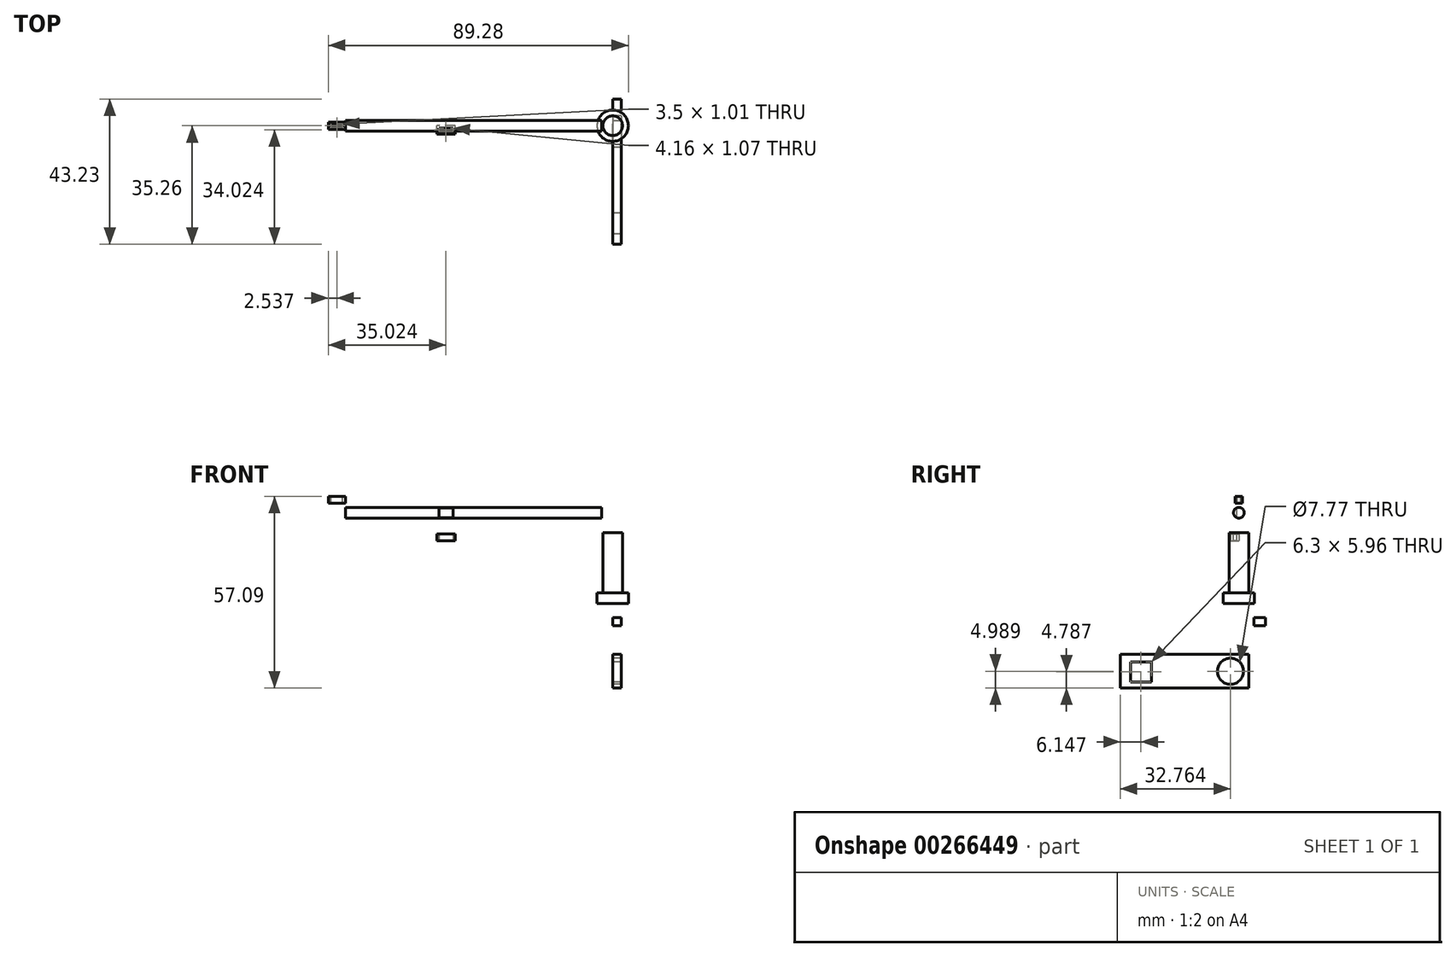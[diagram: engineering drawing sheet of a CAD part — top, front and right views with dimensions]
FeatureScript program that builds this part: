
annotation { "Feature Type Name" : "Feature", "Feature Type Description" : "" }
export const myFeature = defineFeature(function(context is Context, id is Id, definition is map)
    precondition{}
    {
        {
            var Q0;
            Q0=qCreatedBy(makeId("Front.planeOp"),FACE);
            var sketch = newSketch(context, id + "F0", { "sketchPlane" : qUnion([Q0])});
            skLineSegment(sketch, "E0.bottom", {"start": v(-4.66, 21.15) * mm, "end": v(0, 21.15) * mm});
            skLineSegment(sketch, "E0.top", {"start": v(-4.66, 0) * mm, "end": v(0, 0) * mm});
            skLineSegment(sketch, "E0.left", {"start": v(-4.66, 21.15) * mm, "end": v(-4.66, 0) * mm});
            skLineSegment(sketch, "E0.right", {"start": v(0, 21.15) * mm, "end": v(0, 0) * mm});
            skSolve(sketch);
        }
        {
            var Q0;
            Q0=makeQuery(id+"F0.imprint","IMPRINT",FACE,{"disambiguationData":[TD([[makeQuery(id+"F0.imprint","IMPRINT",EDGE,{"derivedFrom":sQuery(id+"F0.wireOp",EDGE,"E0.bottom")}),-1.0]])]});
            var Q1;
            Q1=sQuery(id+"F0.wireOp",EDGE,"E0.right");
            revolve(context, id + "F1", {"entities" : qUnion([Q0]), "axis" : qUnion([Q1]), "revolveType" : RevolveType.FULL});
        }
        {
            var Q0;
            Q0=qCreatedBy(makeId("Front.planeOp"),FACE);
            var sketch = newSketch(context, id + "F2", { "sketchPlane" : qUnion([Q0])});
            skLineSegment(sketch, "E1.bottom", {"start": v(-79.54, 28.67) * mm, "end": v(-3.34, 28.67) * mm});
            skLineSegment(sketch, "E1.top", {"start": v(-79.54, 27.07) * mm, "end": v(-3.34, 27.07) * mm});
            skLineSegment(sketch, "E1.left", {"start": v(-79.54, 28.67) * mm, "end": v(-79.54, 27.07) * mm});
            skLineSegment(sketch, "E1.right", {"start": v(-3.34, 28.67) * mm, "end": v(-3.34, 27.07) * mm});
            skSolve(sketch);
        }
        {
            var Q0;
            Q0=makeQuery(id+"F2.imprint","IMPRINT",FACE,{"disambiguationData":[TD([[makeQuery(id+"F2.imprint","IMPRINT",EDGE,{"derivedFrom":sQuery(id+"F2.wireOp",EDGE,"E1.bottom")}),-1.0]])]});
            var Q1;
            Q1=sQuery(id+"F2.wireOp",EDGE,"E1.top");
            revolve(context, id + "F3", {"entities" : qUnion([Q0]), "axis" : qUnion([Q1]), "revolveType" : RevolveType.FULL});
        }
        {
            var Q0;
            Q0=qCreatedBy(makeId("Front.planeOp"),FACE);
            var sketch = newSketch(context, id + "F4", { "sketchPlane" : qUnion([Q0])});
            skLineSegment(sketch, "E2.bottom", {"start": v(2.93, 21.6) * mm, "end": v(5.43, 21.6) * mm});
            skLineSegment(sketch, "E2.top", {"start": v(2.93, 3.28) * mm, "end": v(5.43, 3.28) * mm});
            skLineSegment(sketch, "E2.left", {"start": v(2.93, 21.6) * mm, "end": v(2.93, 3.28) * mm});
            skLineSegment(sketch, "E2.right", {"start": v(5.43, 21.6) * mm, "end": v(5.43, 3.28) * mm});
            skSolve(sketch);
        }
        {
            var Q0;
            Q0=makeQuery(id+"F4.imprint","IMPRINT",FACE,{"disambiguationData":[TD([[makeQuery(id+"F4.imprint","IMPRINT",EDGE,{"derivedFrom":sQuery(id+"F4.wireOp",EDGE,"E2.bottom")}),-1.0]])]});
            var Q1;
            Q1=makeQuery(id+"F1.opRevolve","SWEPT_FACE",FACE,{"disambiguationData":[OSD([sQuery(id+"F0.wireOp",EDGE,"E0.left")])]});
            revolve(context, id + "F5", {"operationType" : NewBodyOperationType.REMOVE, "entities" : qUnion([Q0]), "axis" : qUnion([Q1]), "revolveType" : RevolveType.FULL, "oppositeDirection" : true});
        }
        {
            var Q0;
            Q0=makeQuery(id+"F3.opRevolve","SWEPT_FACE",FACE,{"disambiguationData":[OSD([sQuery(id+"F2.wireOp",EDGE,"E1.left")])]});
            var sketch = newSketch(context, id + "F6", { "sketchPlane" : qUnion([Q0])});
            skLineSegment(sketch, "E3.bottom", {"start": v(-1.06, 32) * mm, "end": v(1.16, 32) * mm});
            skLineSegment(sketch, "E3.top", {"start": v(-1.06, 29.89) * mm, "end": v(1.16, 29.89) * mm});
            skLineSegment(sketch, "E3.left", {"start": v(-1.06, 32) * mm, "end": v(-1.06, 29.89) * mm});
            skLineSegment(sketch, "E3.right", {"start": v(1.16, 32) * mm, "end": v(1.16, 29.89) * mm});
            skSolve(sketch);
        }
        {
            var Q0;
            Q0=makeQuery(id+"F6.imprint","IMPRINT",FACE,{"disambiguationData":[TD([[makeQuery(id+"F6.imprint","IMPRINT",EDGE,{"derivedFrom":sQuery(id+"F6.wireOp",EDGE,"E3.bottom")}),-1.0]])]});
            extrude(context, id + "F7", {"entities" : qUnion([Q0]), "operationType" : NewBodyOperationType.ADD, "depth" : 5.08 * mm});
        }
        {
            var Q0;
            Q0=makeQuery(id+"F7.opExtrude","SWEPT_FACE",FACE,{"disambiguationData":[OSD([sQuery(id+"F6.wireOp",EDGE,"E3.bottom")])]});
            var sketch = newSketch(context, id + "F8", { "sketchPlane" : qUnion([Q0])});
            skLineSegment(sketch, "E4.bottom", {"start": v(-83.84, 0.5) * mm, "end": v(-80.33, 0.5) * mm});
            skLineSegment(sketch, "E4.top", {"start": v(-83.84, -0.5) * mm, "end": v(-80.33, -0.5) * mm});
            skLineSegment(sketch, "E4.left", {"start": v(-83.84, 0.5) * mm, "end": v(-83.84, -0.5) * mm});
            skLineSegment(sketch, "E4.right", {"start": v(-80.33, 0.5) * mm, "end": v(-80.33, -0.5) * mm});
            skPoint(sketch, "E4.middle", {"position": v(-82.08, 0) * mm});
            skPoint(sketch, "E4.middle.positionSnap0", {"position": v(-82.08, -1.16) * mm});
            skPoint(sketch, "E4.centerSnap0", {"position": v(-82.08, -1.16) * mm});
            skSolve(sketch);
        }
        {
            var Q0;
            Q0=makeQuery(id+"F8.imprint","IMPRINT",FACE,{"disambiguationData":[TD([[makeQuery(id+"F8.imprint","IMPRINT",EDGE,{"derivedFrom":sQuery(id+"F8.wireOp",EDGE,"E4.bottom")}),-1.0]])]});
            extrude(context, id + "F9", {"entities" : qUnion([Q0]), "operationType" : NewBodyOperationType.REMOVE, "endBound" : BoundingType.THROUGH_ALL, "oppositeDirection" : true, "depth" : 25.4 * mm});
        }
        {
            var Q0;
            Q0=qCreatedBy(makeId("Right.planeOp"),FACE);
            var sketch = newSketch(context, id + "F10", { "sketchPlane" : qUnion([Q0])});
            skLineSegment(sketch, "E5.bottom", {"start": v(3.02, -15.1) * mm, "end": v(-35.26, -15.1) * mm});
            skLineSegment(sketch, "E5.top", {"start": v(3.02, -25.1) * mm, "end": v(-35.26, -25.1) * mm});
            skLineSegment(sketch, "E5.left", {"start": v(3.02, -15.1) * mm, "end": v(3.02, -25.1) * mm});
            skLineSegment(sketch, "E5.right", {"start": v(-35.26, -15.1) * mm, "end": v(-35.26, -25.1) * mm});
            skCircle(sketch, "E6", {"center": v(-2.5, -20.1) * mm, "radius": 3.89 * mm});
            skLineSegment(sketch, "E7.bottom", {"start": v(-32.26, -17.33) * mm, "end": v(-25.96, -17.33) * mm});
            skLineSegment(sketch, "E7.top", {"start": v(-32.26, -23.28) * mm, "end": v(-25.96, -23.28) * mm});
            skLineSegment(sketch, "E7.left", {"start": v(-32.26, -17.33) * mm, "end": v(-32.26, -23.28) * mm});
            skLineSegment(sketch, "E7.right", {"start": v(-25.96, -17.33) * mm, "end": v(-25.96, -23.28) * mm});
            skSolve(sketch);
        }
        {
            var Q0;
            Q0 = qSketchRegion(id + "F10", true);
            extrude(context, id + "F11", {"entities" : qUnion([Q0]), "depth" : 2.54 * mm});
        }
        {
            var Q0;
            Q0=qCreatedBy(makeId("Right.planeOp"),FACE);
            var sketch = newSketch(context, id + "F12", { "sketchPlane" : qUnion([Q0])});
            skLineSegment(sketch, "E8.bottom", {"start": v(4.47, -4.08) * mm, "end": v(7.97, -4.08) * mm});
            skLineSegment(sketch, "E8.top", {"start": v(4.47, -6.57) * mm, "end": v(7.97, -6.57) * mm});
            skLineSegment(sketch, "E8.left", {"start": v(4.47, -4.08) * mm, "end": v(4.47, -6.57) * mm});
            skLineSegment(sketch, "E8.right", {"start": v(7.97, -4.08) * mm, "end": v(7.97, -6.57) * mm});
            skSolve(sketch);
        }
        {
            var Q0;
            Q0=makeQuery(id+"F12.imprint","IMPRINT",FACE,{"disambiguationData":[TD([[makeQuery(id+"F12.imprint","IMPRINT",EDGE,{"derivedFrom":sQuery(id+"F12.wireOp",EDGE,"E8.bottom")}),-1.0]])]});
            extrude(context, id + "F13", {"entities" : qUnion([Q0]), "depth" : 2.54 * mm});
        }
        {
            var Q0;
            Q0=qCreatedBy(makeId("Front.planeOp"),FACE);
            var sketch = newSketch(context, id + "F14", { "sketchPlane" : qUnion([Q0])});
            skLineSegment(sketch, "E9.bottom", {"start": v(-46.86, 20.72) * mm, "end": v(-52.33, 20.72) * mm});
            skLineSegment(sketch, "E9.top", {"start": v(-46.86, 18.68) * mm, "end": v(-52.33, 18.68) * mm});
            skLineSegment(sketch, "E9.left", {"start": v(-46.86, 20.72) * mm, "end": v(-46.86, 18.68) * mm});
            skLineSegment(sketch, "E9.right", {"start": v(-52.33, 20.72) * mm, "end": v(-52.33, 18.68) * mm});
            skSolve(sketch);
        }
        {
            var Q0;
            Q0=makeQuery(id+"F14.imprint","IMPRINT",FACE,{"disambiguationData":[TD([[makeQuery(id+"F14.imprint","IMPRINT",EDGE,{"derivedFrom":sQuery(id+"F14.wireOp",EDGE,"E9.bottom")}),1.0]])]});
            extrude(context, id + "F15", {"entities" : qUnion([Q0]), "depth" : 2.54 * mm});
        }
        {
            var Q0;
            Q0=makeQuery(id+"F15.opExtrude","SWEPT_FACE",FACE,{"disambiguationData":[OSD([sQuery(id+"F14.wireOp",EDGE,"E9.top")])]});
            var sketch = newSketch(context, id + "F16", { "sketchPlane" : qUnion([Q0])});
            skLineSegment(sketch, "E10.bottom", {"start": v(-47.52, 0.7) * mm, "end": v(-51.67, 0.7) * mm});
            skLineSegment(sketch, "E10.top", {"start": v(-47.52, 1.77) * mm, "end": v(-51.67, 1.77) * mm});
            skLineSegment(sketch, "E10.left", {"start": v(-47.52, 0.7) * mm, "end": v(-47.52, 1.77) * mm});
            skLineSegment(sketch, "E10.right", {"start": v(-51.67, 0.7) * mm, "end": v(-51.67, 1.77) * mm});
            skSolve(sketch);
        }
        {
            var Q0;
            Q0=makeQuery(id+"F16.imprint","IMPRINT",FACE,{"disambiguationData":[TD([[makeQuery(id+"F16.imprint","IMPRINT",EDGE,{"derivedFrom":sQuery(id+"F16.wireOp",EDGE,"E10.bottom")}),-1.0]])]});
            extrude(context, id + "F17", {"entities" : qUnion([Q0]), "operationType" : NewBodyOperationType.REMOVE, "endBound" : BoundingType.THROUGH_ALL, "oppositeDirection" : true, "depth" : 25.4 * mm});
        }
    });
